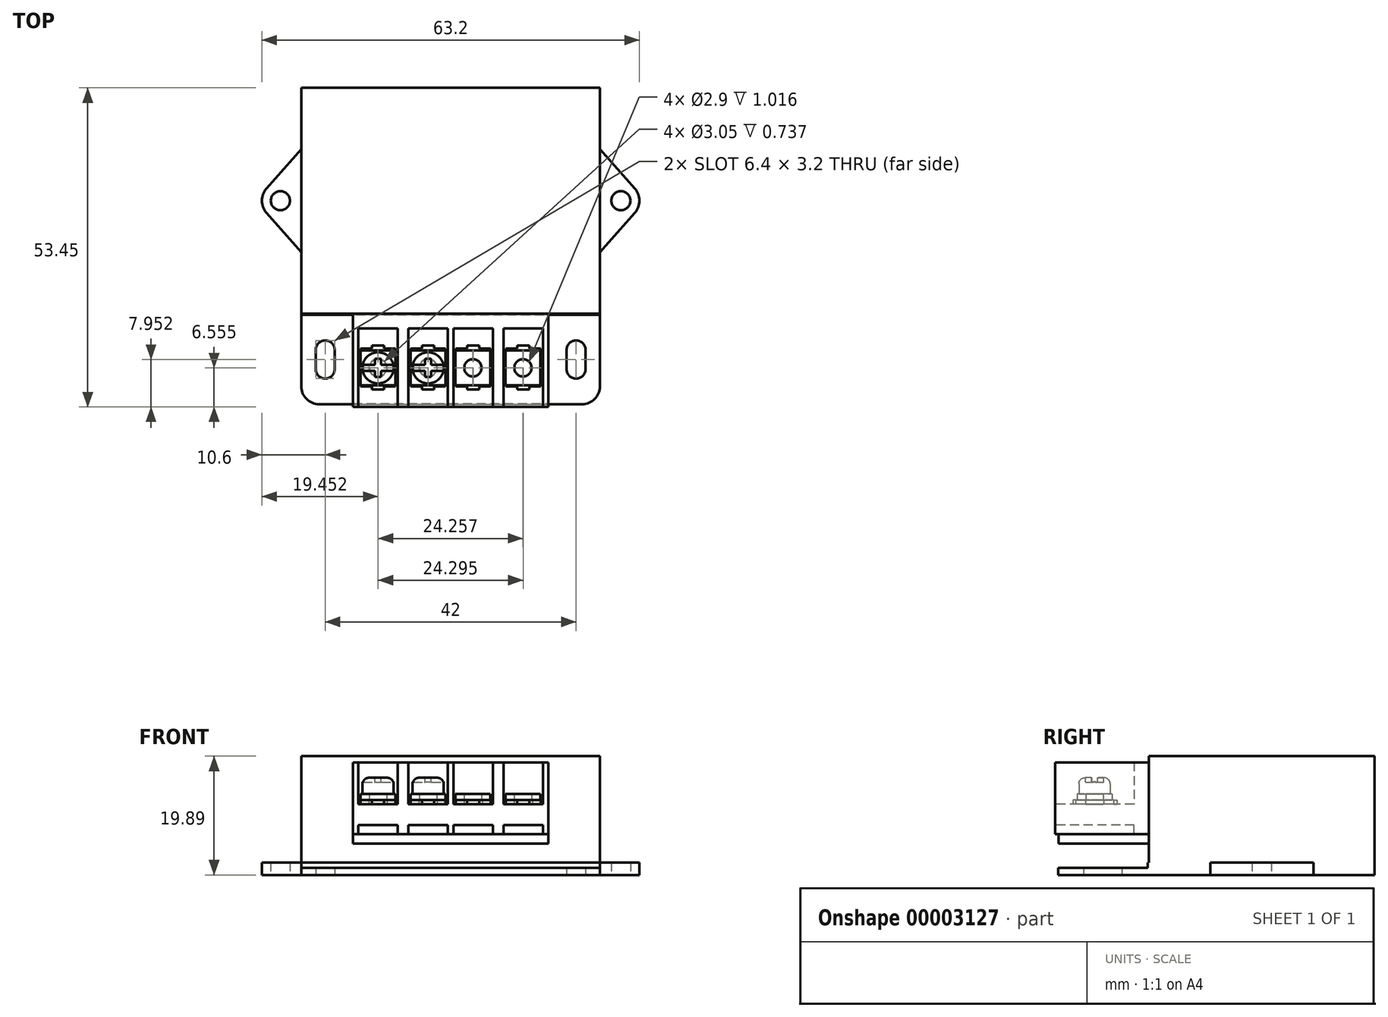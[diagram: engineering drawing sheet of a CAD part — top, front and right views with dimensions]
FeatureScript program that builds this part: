
annotation { "Feature Type Name" : "Feature", "Feature Type Description" : "" }
export const myFeature = defineFeature(function(context is Context, id is Id, definition is map)
    precondition{}
    {
        {
            var Q0;
            Q0=qCreatedBy(makeId("Top.planeOp"),FACE);
            var sketch = newSketch(context, id + "F0", { "sketchPlane" : qUnion([Q0])});
            skLineSegment(sketch, "E0.rect.bottom", {"start": v(0, -19.1) * mm, "end": v(-25, -19.1) * mm});
            skLineSegment(sketch, "E0.rect.top", {"start": v(0, 18.9) * mm, "end": v(-25, 18.9) * mm});
            skLineSegment(sketch, "E0.rect.right", {"start": v(-25, -19.1) * mm, "end": v(-25, -8.64) * mm});
            skPoint(sketch, "E0.rect.middle", {"position": v(0, 0) * mm});
            skLineSegment(sketch, "E1", {"start": v(0, 28.46) * mm, "end": v(0, -30.31) * mm, "construction": true});
            skLineSegment(sketch, "E2", {"start": v(-25, 8.64) * mm, "end": v(-30.82, 2.05) * mm});
            skLineSegment(sketch, "E3", {"start": v(-30.82, -2.05) * mm, "end": v(-25, -8.64) * mm});
            skCircle(sketch, "E4", {"center": v(-28.5, 0) * mm, "radius": 1.6 * mm});
            skArc(sketch, "E5", {"start": v(-30.82, 2.05) * mm, "mid": v(-31.6, 0) * mm, "end": v(-30.82, -2.05) * mm});
            skArc(sketch, "E6.0.MirrorCS", {"start": v(30.82, 2.05) * mm, "mid": v(31.6, 0) * mm, "end": v(30.82, -2.05) * mm});
            skCircle(sketch, "E6.1.MirrorC", {"center": v(28.5, 0) * mm, "radius": 1.6 * mm});
            skLineSegment(sketch, "E6.2.MirrorCS", {"start": v(25, -19.1) * mm, "end": v(25, -8.64) * mm});
            skLineSegment(sketch, "E6.3.MirrorCS", {"start": v(25, 8.64) * mm, "end": v(30.82, 2.05) * mm});
            skLineSegment(sketch, "E6.4.MirrorCS", {"start": v(30.82, -2.05) * mm, "end": v(25, -8.64) * mm});
            skLineSegment(sketch, "E7.0.MirrorCS", {"start": v(0, 18.9) * mm, "end": v(25, 18.9) * mm});
            skLineSegment(sketch, "E8.0.MirrorCS", {"start": v(0, -19.1) * mm, "end": v(25, -19.1) * mm});
            skLineSegment(sketch, "E9.trimOffspring", {"start": v(-25, 8.64) * mm, "end": v(-25, 18.9) * mm});
            skLineSegment(sketch, "E10.trimOffspring", {"start": v(25, 8.64) * mm, "end": v(25, 18.9) * mm});
            skSolve(sketch);
        }
        {
            var Q0;
            Q0=makeQuery(id+"F0.imprint","IMPRINT",FACE,{"disambiguationData":[TD([[makeQuery(id+"F0.imprint","IMPRINT",EDGE,{"derivedFrom":sQuery(id+"F0.wireOp",EDGE,"E0.rect.bottom")}),-1.0]])]});
            extrude(context, id + "F1", {"entities" : qUnion([Q0]), "depth" : 2.08 * mm});
        }
        {
            var Q0;
            Q0=makeQuery(id+"F1.opExtrude","CAP_FACE",FACE,{"disambiguationData":[OSD([sQuery(id+"F0.wireOp",EDGE,"E0.rect.bottom"),sQuery(id+"F0.wireOp",EDGE,"E0.rect.right"),sQuery(id+"F0.wireOp",EDGE,"E2"),sQuery(id+"F0.wireOp",EDGE,"E3"),sQuery(id+"F0.wireOp",EDGE,"E4"),sQuery(id+"F0.wireOp",EDGE,"E5"),sQuery(id+"F0.wireOp",EDGE,"E6.0.MirrorCS"),sQuery(id+"F0.wireOp",EDGE,"E6.1.MirrorC"),sQuery(id+"F0.wireOp",EDGE,"E6.2.MirrorCS"),sQuery(id+"F0.wireOp",EDGE,"E6.3.MirrorCS"),sQuery(id+"F0.wireOp",EDGE,"E6.4.MirrorCS"),sQuery(id+"F0.wireOp",EDGE,"E7.0.MirrorCS"),sQuery(id+"F0.wireOp",EDGE,"E9.trimOffspring"),sQuery(id+"F0.wireOp",EDGE,"E10.trimOffspring")])],"isStart":false});
            var sketch = newSketch(context, id + "F2", { "sketchPlane" : qUnion([Q0])});
            skLineSegment(sketch, "E11.rect.bottom", {"start": v(25, 18.9) * mm, "end": v(-25, 18.9) * mm});
            skLineSegment(sketch, "E11.rect.top", {"start": v(25, -18.9) * mm, "end": v(-25, -18.9) * mm});
            skLineSegment(sketch, "E11.rect.left", {"start": v(25, 18.9) * mm, "end": v(25, -18.9) * mm});
            skLineSegment(sketch, "E11.rect.right", {"start": v(-25, 18.9) * mm, "end": v(-25, -18.9) * mm});
            skPoint(sketch, "E11.rect.middle", {"position": v(0, 0) * mm});
            skSolve(sketch);
        }
        {
            var Q0;
            {var subQ2=sQuery(id+"F2.wireOp",EDGE,"E11.rect.bottom");Q0=makeQuery(id+"F2.imprint","IMPRINT",FACE,{"disambiguationData":[TD([[makeQuery(id+"F2.imprint","IMPRINT",EDGE,{"derivedFrom":subQ2}),-1.0]])]});}
            extrude(context, id + "F3", {"entities" : qUnion([Q0]), "operationType" : NewBodyOperationType.ADD, "depth" : 17.8 * mm});
        }
        {
            var Q0;
            Q0=qCreatedBy(makeId("Top.planeOp"),FACE);
            var sketch = newSketch(context, id + "F4", { "sketchPlane" : qUnion([Q0])});
            skLineSegment(sketch, "E12.bottom", {"start": v(-25, -19.1) * mm, "end": v(0, -19.1) * mm});
            skLineSegment(sketch, "E12.top", {"start": v(-22, -34.1) * mm, "end": v(0, -34.1) * mm});
            skLineSegment(sketch, "E12.left", {"start": v(-25, -19.1) * mm, "end": v(-25, -31.1) * mm});
            skPoint(sketch, "E13.visualSharp", {"position": v(-25, -34.1) * mm});
            skArc(sketch, "E13.filletArc", {"start": v(-25, -31.1) * mm, "mid": v(-24.12, -33.22) * mm, "end": v(-22, -34.1) * mm});
            skLineSegment(sketch, "E14", {"start": v(0, 0) * mm, "end": v(0, -41.86) * mm, "construction": true});
            skArc(sketch, "E15", {"start": v(-19.4, -25) * mm, "mid": v(-21, -23.4) * mm, "end": v(-22.6, -25) * mm});
            skArc(sketch, "E16", {"start": v(-22.6, -28.2) * mm, "mid": v(-21, -29.8) * mm, "end": v(-19.4, -28.2) * mm});
            skLineSegment(sketch, "E17", {"start": v(-27.88, -26.6) * mm, "end": v(-15.03, -26.6) * mm, "construction": true});
            skLineSegment(sketch, "E18", {"start": v(-22.6, -25) * mm, "end": v(-22.6, -28.2) * mm});
            skLineSegment(sketch, "E19", {"start": v(-19.4, -25) * mm, "end": v(-19.4, -28.2) * mm});
            skLineSegment(sketch, "E20.0.MirrorCS", {"start": v(-25, -19.1) * mm, "end": v(-25, -7.1) * mm});
            skArc(sketch, "E21.0.MirrorCS", {"start": v(-25, -7.1) * mm, "mid": v(-24.12, -4.98) * mm, "end": v(-22, -4.1) * mm});
            skLineSegment(sketch, "E22.0.MirrorCS", {"start": v(-22, -4.1) * mm, "end": v(0, -4.1) * mm});
            skArc(sketch, "E23.0.MirrorCS", {"start": v(-22.6, -10) * mm, "mid": v(-21, -8.4) * mm, "end": v(-19.4, -10) * mm});
            skLineSegment(sketch, "E24.0.MirrorCS", {"start": v(-19.4, -13.2) * mm, "end": v(-19.4, -10) * mm});
            skArc(sketch, "E25.0.MirrorCS", {"start": v(-19.4, -13.2) * mm, "mid": v(-21, -14.8) * mm, "end": v(-22.6, -13.2) * mm});
            skLineSegment(sketch, "E26.0.MirrorCS", {"start": v(22, -34.1) * mm, "end": v(0, -34.1) * mm});
            skArc(sketch, "E26.1.MirrorCS", {"start": v(25, -31.1) * mm, "mid": v(24.12, -33.22) * mm, "end": v(22, -34.1) * mm});
            skArc(sketch, "E26.2.MirrorCS", {"start": v(22.6, -28.2) * mm, "mid": v(21, -29.8) * mm, "end": v(19.4, -28.2) * mm});
            skLineSegment(sketch, "E26.3.MirrorCS", {"start": v(19.4, -25) * mm, "end": v(19.4, -28.2) * mm});
            skLineSegment(sketch, "E26.4.MirrorCS", {"start": v(22.6, -25) * mm, "end": v(22.6, -28.2) * mm});
            skArc(sketch, "E26.5.MirrorCS", {"start": v(19.4, -25) * mm, "mid": v(21, -23.4) * mm, "end": v(22.6, -25) * mm});
            skLineSegment(sketch, "E26.6.MirrorCS", {"start": v(25, -19.1) * mm, "end": v(0, -19.1) * mm});
            skLineSegment(sketch, "E26.7.MirrorCS", {"start": v(25, -19.1) * mm, "end": v(25, -31.1) * mm});
            skSolve(sketch);
        }
        {
            var Q0;
            Q0=makeQuery(id+"F4.imprint","IMPRINT",FACE,{"disambiguationData":[TD([[makeQuery(id+"F4.imprint","IMPRINT",EDGE,{"derivedFrom":sQuery(id+"F4.wireOp",EDGE,"E12.bottom")}),-1.0]])]});
            extrude(context, id + "F5", {"entities" : qUnion([Q0]), "operationType" : NewBodyOperationType.ADD, "depth" : 1.2 * mm});
        }
        {
            var Q0;
            Q0=makeQuery(id+"F3.opExtrude","SWEPT_FACE",FACE,{"disambiguationData":[OSD([sQuery(id+"F2.wireOp",EDGE,"E11.rect.top")])]});
            var sketch = newSketch(context, id + "F6", { "sketchPlane" : qUnion([Q0])});
            skLineSegment(sketch, "E27.bottom", {"start": v(-16.34, 18.85) * mm, "end": v(0, 18.85) * mm});
            skLineSegment(sketch, "E27.top", {"start": v(-16.34, 6.86) * mm, "end": v(0, 6.86) * mm});
            skLineSegment(sketch, "E27.left", {"start": v(-16.34, 18.85) * mm, "end": v(-16.34, 6.86) * mm});
            skLineSegment(sketch, "E28", {"start": v(0, 2.87) * mm, "end": v(0, 22.04) * mm, "construction": true});
            skLineSegment(sketch, "E29.0.MirrorCS", {"start": v(16.34, 18.85) * mm, "end": v(0, 18.85) * mm});
            skLineSegment(sketch, "E30.0.MirrorCS", {"start": v(16.34, 18.85) * mm, "end": v(16.34, 6.86) * mm});
            skLineSegment(sketch, "E31.0.MirrorCS", {"start": v(16.34, 6.86) * mm, "end": v(0, 6.86) * mm});
            skSolve(sketch);
        }
        {
            var Q0;
            Q0=makeQuery(id+"F6.imprint","IMPRINT",FACE,{"disambiguationData":[TD([[makeQuery(id+"F6.imprint","IMPRINT",EDGE,{"derivedFrom":sQuery(id+"F6.wireOp",EDGE,"E27.bottom")}),-1.0]])]});
            extrude(context, id + "F7", {"entities" : qUnion([Q0]), "depth" : 15.65 * mm});
        }
        {
            var Q0;
            Q0=makeQuery(id+"F7.opExtrude","CAP_FACE",FACE,{"disambiguationData":[OSD([sQuery(id+"F6.wireOp",EDGE,"E27.bottom"),sQuery(id+"F6.wireOp",EDGE,"E27.top"),sQuery(id+"F6.wireOp",EDGE,"E27.left"),sQuery(id+"F6.wireOp",EDGE,"E29.0.MirrorCS"),sQuery(id+"F6.wireOp",EDGE,"E30.0.MirrorCS"),sQuery(id+"F6.wireOp",EDGE,"E31.0.MirrorCS")])],"isStart":false});
            var sketch = newSketch(context, id + "F8", { "sketchPlane" : qUnion([Q0])});
            skLineSegment(sketch, "E32.bottom", {"start": v(-15.45, 18.85) * mm, "end": v(-8.85, 18.85) * mm});
            skLineSegment(sketch, "E32.top", {"start": v(-15.45, 11.84) * mm, "end": v(-8.85, 11.84) * mm});
            skLineSegment(sketch, "E32.left", {"start": v(-15.45, 18.85) * mm, "end": v(-15.45, 11.84) * mm});
            skLineSegment(sketch, "E32.right", {"start": v(-8.85, 18.85) * mm, "end": v(-8.85, 11.84) * mm});
            skLineSegment(sketch, "E33.bottom", {"start": v(-7.07, 18.85) * mm, "end": v(-0.46, 18.85) * mm});
            skLineSegment(sketch, "E33.top", {"start": v(-7.07, 11.84) * mm, "end": v(-0.46, 11.84) * mm});
            skLineSegment(sketch, "E33.left", {"start": v(-7.07, 18.85) * mm, "end": v(-7.07, 11.84) * mm});
            skLineSegment(sketch, "E33.right", {"start": v(-0.46, 18.85) * mm, "end": v(-0.46, 11.84) * mm});
            skLineSegment(sketch, "E34", {"start": v(0, 23) * mm, "end": v(0, -5.26) * mm, "construction": true});
            skLineSegment(sketch, "E35.0.MirrorCS", {"start": v(7.07, 18.85) * mm, "end": v(0.46, 18.85) * mm});
            skLineSegment(sketch, "E36.0.MirrorCS", {"start": v(7.07, 18.85) * mm, "end": v(7.07, 11.84) * mm});
            skLineSegment(sketch, "E37.0.MirrorCS", {"start": v(0.46, 18.85) * mm, "end": v(0.46, 11.84) * mm});
            skLineSegment(sketch, "E38.0.MirrorCS", {"start": v(7.07, 11.84) * mm, "end": v(0.46, 11.84) * mm});
            skLineSegment(sketch, "E39.0.MirrorCS", {"start": v(8.85, 18.85) * mm, "end": v(8.85, 11.84) * mm});
            skLineSegment(sketch, "E40.0.MirrorCS", {"start": v(15.45, 18.85) * mm, "end": v(8.85, 18.85) * mm});
            skLineSegment(sketch, "E41.0.MirrorCS", {"start": v(15.45, 18.85) * mm, "end": v(15.45, 11.84) * mm});
            skLineSegment(sketch, "E42.0.MirrorCS", {"start": v(15.45, 11.84) * mm, "end": v(8.85, 11.84) * mm});
            skLineSegment(sketch, "E43.bottom", {"start": v(-15.45, 6.86) * mm, "end": v(-8.85, 6.86) * mm});
            skLineSegment(sketch, "E43.top", {"start": v(-15.45, 8.36) * mm, "end": v(-8.85, 8.36) * mm});
            skLineSegment(sketch, "E43.left", {"start": v(-15.45, 6.86) * mm, "end": v(-15.45, 8.36) * mm});
            skLineSegment(sketch, "E43.right", {"start": v(-8.85, 6.86) * mm, "end": v(-8.85, 8.36) * mm});
            skLineSegment(sketch, "E44.bottom", {"start": v(-7.07, 6.86) * mm, "end": v(-0.46, 6.86) * mm});
            skLineSegment(sketch, "E44.top", {"start": v(-7.07, 8.36) * mm, "end": v(-0.46, 8.36) * mm});
            skLineSegment(sketch, "E44.left", {"start": v(-7.07, 6.86) * mm, "end": v(-7.07, 8.36) * mm});
            skLineSegment(sketch, "E44.right", {"start": v(-0.46, 6.86) * mm, "end": v(-0.46, 8.36) * mm});
            skLineSegment(sketch, "E45.0.MirrorCS", {"start": v(15.45, 6.86) * mm, "end": v(8.85, 6.86) * mm});
            skLineSegment(sketch, "E45.1.MirrorCS", {"start": v(0.46, 6.86) * mm, "end": v(0.46, 8.36) * mm});
            skLineSegment(sketch, "E45.2.MirrorCS", {"start": v(7.07, 6.86) * mm, "end": v(7.07, 8.36) * mm});
            skLineSegment(sketch, "E45.3.MirrorCS", {"start": v(15.45, 6.86) * mm, "end": v(15.45, 8.36) * mm});
            skLineSegment(sketch, "E45.4.MirrorCS", {"start": v(15.45, 8.36) * mm, "end": v(8.85, 8.36) * mm});
            skLineSegment(sketch, "E45.5.MirrorCS", {"start": v(7.07, 6.86) * mm, "end": v(0.46, 6.86) * mm});
            skLineSegment(sketch, "E45.6.MirrorCS", {"start": v(7.07, 8.36) * mm, "end": v(0.46, 8.36) * mm});
            skLineSegment(sketch, "E45.7.MirrorCS", {"start": v(8.85, 6.86) * mm, "end": v(8.85, 8.36) * mm});
            skSolve(sketch);
        }
        {
            var Q0;
            {Q0=qUnion([makeQuery(id+"F8.imprint","IMPRINT",FACE,{"disambiguationData":[TD([[makeQuery(id+"F8.imprint","IMPRINT",EDGE,{"derivedFrom":sQuery(id+"F8.wireOp",EDGE,"E32.bottom")}),-1.0]])]}),makeQuery(id+"F8.imprint","IMPRINT",FACE,{"disambiguationData":[TD([[makeQuery(id+"F8.imprint","IMPRINT",EDGE,{"derivedFrom":sQuery(id+"F8.wireOp",EDGE,"E33.bottom")}),-1.0]])]}),makeQuery(id+"F8.imprint","IMPRINT",FACE,{"disambiguationData":[TD([[makeQuery(id+"F8.imprint","IMPRINT",EDGE,{"derivedFrom":sQuery(id+"F8.wireOp",EDGE,"E35.0.MirrorCS")}),-1.0]])]}),makeQuery(id+"F8.imprint","IMPRINT",FACE,{"disambiguationData":[TD([[makeQuery(id+"F8.imprint","IMPRINT",EDGE,{"derivedFrom":sQuery(id+"F8.wireOp",EDGE,"E39.0.MirrorCS")}),1.0]])]}),makeQuery(id+"F8.imprint","IMPRINT",FACE,{"disambiguationData":[TD([[makeQuery(id+"F8.imprint","IMPRINT",EDGE,{"derivedFrom":sQuery(id+"F8.wireOp",EDGE,"E43.bottom")}),1.0]])]}),makeQuery(id+"F8.imprint","IMPRINT",FACE,{"disambiguationData":[TD([[makeQuery(id+"F8.imprint","IMPRINT",EDGE,{"derivedFrom":sQuery(id+"F8.wireOp",EDGE,"E44.bottom")}),1.0]])]}),makeQuery(id+"F8.imprint","IMPRINT",FACE,{"disambiguationData":[TD([[makeQuery(id+"F8.imprint","IMPRINT",EDGE,{"derivedFrom":sQuery(id+"F8.wireOp",EDGE,"E45.0.MirrorCS")}),1.0]])]}),makeQuery(id+"F8.imprint","IMPRINT",FACE,{"disambiguationData":[TD([[makeQuery(id+"F8.imprint","IMPRINT",EDGE,{"derivedFrom":sQuery(id+"F8.wireOp",EDGE,"E45.1.MirrorCS")}),-1.0]])]})]);}
            extrude(context, id + "F9", {"entities" : qUnion([Q0]), "operationType" : NewBodyOperationType.REMOVE, "oppositeDirection" : true, "depth" : 13.16 * mm});
        }
        {
            var Q0;
            Q0=makeQuery(id+"F3.opExtrude","SWEPT_FACE",FACE,{"disambiguationData":[OSD([sQuery(id+"F2.wireOp",EDGE,"E11.rect.top")])]});
            var sketch = newSketch(context, id + "F10", { "sketchPlane" : qUnion([Q0])});
            skLineSegment(sketch, "E46", {"start": v(0, 20.95) * mm, "end": v(0, -1.51) * mm, "construction": true});
            skLineSegment(sketch, "E47", {"start": v(0, 6.86) * mm, "end": v(-16.33, 6.86) * mm});
            skLineSegment(sketch, "E48", {"start": v(-16.33, 6.86) * mm, "end": v(-16.33, 5.23) * mm});
            skLineSegment(sketch, "E49", {"start": v(-16.33, 5.23) * mm, "end": v(0, 5.23) * mm});
            skLineSegment(sketch, "E50.0.MirrorCS", {"start": v(16.33, 5.23) * mm, "end": v(0, 5.23) * mm});
            skLineSegment(sketch, "E51.0.MirrorCS", {"start": v(0, 6.86) * mm, "end": v(16.33, 6.86) * mm});
            skLineSegment(sketch, "E52.0.MirrorCS", {"start": v(16.33, 6.86) * mm, "end": v(16.33, 5.23) * mm});
            skSolve(sketch);
        }
        {
            var Q0;
            Q0=makeQuery(id+"F10.imprint","IMPRINT",FACE,{"disambiguationData":[TD([[makeQuery(id+"F10.imprint","IMPRINT",EDGE,{"derivedFrom":sQuery(id+"F10.wireOp",EDGE,"E47")}),1.0]])]});
            var Q1;
            Q1=makeQuery(id+"F7.opExtrude","CAP_FACE",FACE,{"disambiguationData":[OSD([sQuery(id+"F6.wireOp",EDGE,"E27.bottom"),sQuery(id+"F6.wireOp",EDGE,"E27.top"),sQuery(id+"F6.wireOp",EDGE,"E27.left"),sQuery(id+"F6.wireOp",EDGE,"E29.0.MirrorCS"),sQuery(id+"F6.wireOp",EDGE,"E30.0.MirrorCS"),sQuery(id+"F6.wireOp",EDGE,"E31.0.MirrorCS")])],"isStart":false});
            extrude(context, id + "F11", {"entities" : qUnion([Q0]), "endBoundEntity" : qUnion([Q1]), "depth" : 15.1 * mm});
        }
        {
            var Q0;
            Q0=makeQuery(id+"F9.boolean.opBoolean","COPY",FACE,{"derivedFrom":makeQuery(id+"F9.opExtrude","SWEPT_FACE",FACE,{"disambiguationData":[OSD([sQuery(id+"F8.wireOp",EDGE,"E32.top")])]})});
            var sketch = newSketch(context, id + "F12", { "sketchPlane" : qUnion([Q0])});
            skLineSegment(sketch, "E53.bottom", {"start": v(-15.07, -24.77) * mm, "end": v(-13.16, -24.77) * mm});
            skLineSegment(sketch, "E53.top", {"start": v(-15.07, -31.12) * mm, "end": v(-13.16, -31.12) * mm});
            skLineSegment(sketch, "E53.left", {"start": v(-15.07, -24.77) * mm, "end": v(-15.07, -31.12) * mm});
            skLineSegment(sketch, "E53.right", {"start": v(-9.23, -24.77) * mm, "end": v(-9.23, -31.12) * mm});
            skLineSegment(sketch, "E54.bottom", {"start": v(-6.69, -24.77) * mm, "end": v(-4.78, -24.77) * mm});
            skLineSegment(sketch, "E54.top", {"start": v(-6.69, -31.12) * mm, "end": v(-4.78, -31.12) * mm});
            skLineSegment(sketch, "E54.left", {"start": v(-6.69, -24.77) * mm, "end": v(-6.69, -31.12) * mm});
            skLineSegment(sketch, "E54.right", {"start": v(-0.84, -24.77) * mm, "end": v(-0.84, -31.12) * mm});
            skLineSegment(sketch, "E55", {"start": v(-12.15, -21.4) * mm, "end": v(-12.15, -41.65) * mm, "construction": true});
            skLineSegment(sketch, "E56", {"start": v(-3.77, -21.7) * mm, "end": v(-3.77, -39.4) * mm, "construction": true});
            skLineSegment(sketch, "E57", {"start": v(0, -15.65) * mm, "end": v(0, -38.77) * mm, "construction": true});
            skLineSegment(sketch, "E58.top", {"start": v(-13.16, -24.26) * mm, "end": v(-11.13, -24.26) * mm});
            skLineSegment(sketch, "E58.left", {"start": v(-13.16, -24.77) * mm, "end": v(-13.16, -24.26) * mm});
            skLineSegment(sketch, "E58.right", {"start": v(-11.13, -24.77) * mm, "end": v(-11.13, -24.26) * mm});
            skLineSegment(sketch, "E59.top", {"start": v(-13.16, -31.63) * mm, "end": v(-11.13, -31.63) * mm});
            skLineSegment(sketch, "E59.left", {"start": v(-13.16, -31.12) * mm, "end": v(-13.16, -31.63) * mm});
            skLineSegment(sketch, "E59.right", {"start": v(-11.13, -31.12) * mm, "end": v(-11.13, -31.63) * mm});
            skLineSegment(sketch, "E60.top", {"start": v(-4.78, -24.26) * mm, "end": v(-2.75, -24.26) * mm});
            skLineSegment(sketch, "E60.left", {"start": v(-4.78, -24.77) * mm, "end": v(-4.78, -24.26) * mm});
            skLineSegment(sketch, "E60.right", {"start": v(-2.75, -24.77) * mm, "end": v(-2.75, -24.26) * mm});
            skLineSegment(sketch, "E61.top", {"start": v(-4.78, -31.63) * mm, "end": v(-2.75, -31.63) * mm});
            skLineSegment(sketch, "E61.left", {"start": v(-4.78, -31.12) * mm, "end": v(-4.78, -31.63) * mm});
            skLineSegment(sketch, "E61.right", {"start": v(-2.75, -31.12) * mm, "end": v(-2.75, -31.63) * mm});
            skLineSegment(sketch, "E62.trimOffspring", {"start": v(-11.13, -24.77) * mm, "end": v(-9.23, -24.77) * mm});
            skLineSegment(sketch, "E63.trimOffspring", {"start": v(-11.13, -31.12) * mm, "end": v(-9.23, -31.12) * mm});
            skLineSegment(sketch, "E64.trimOffspring", {"start": v(-2.75, -31.12) * mm, "end": v(-0.84, -31.12) * mm});
            skLineSegment(sketch, "E65.trimOffspring", {"start": v(-2.75, -24.77) * mm, "end": v(-0.84, -24.77) * mm});
            skLineSegment(sketch, "E66.0.MirrorCS", {"start": v(11.13, -31.12) * mm, "end": v(11.13, -31.63) * mm});
            skLineSegment(sketch, "E66.1.MirrorCS", {"start": v(2.75, -24.77) * mm, "end": v(0.84, -24.77) * mm});
            skLineSegment(sketch, "E66.2.MirrorCS", {"start": v(2.75, -31.12) * mm, "end": v(2.75, -31.63) * mm});
            skLineSegment(sketch, "E66.3.MirrorCS", {"start": v(11.13, -31.12) * mm, "end": v(9.23, -31.12) * mm});
            skLineSegment(sketch, "E66.4.MirrorCS", {"start": v(11.13, -24.77) * mm, "end": v(11.13, -24.26) * mm});
            skLineSegment(sketch, "E66.5.MirrorCS", {"start": v(4.78, -24.77) * mm, "end": v(4.78, -24.26) * mm});
            skLineSegment(sketch, "E66.6.MirrorCS", {"start": v(4.78, -31.63) * mm, "end": v(2.75, -31.63) * mm});
            skLineSegment(sketch, "E66.7.MirrorCS", {"start": v(4.78, -31.12) * mm, "end": v(4.78, -31.63) * mm});
            skLineSegment(sketch, "E66.8.MirrorCS", {"start": v(13.16, -24.26) * mm, "end": v(11.13, -24.26) * mm});
            skLineSegment(sketch, "E66.9.MirrorCS", {"start": v(6.69, -24.77) * mm, "end": v(6.69, -31.12) * mm});
            skLineSegment(sketch, "E66.10.MirrorCS", {"start": v(0.84, -24.77) * mm, "end": v(0.84, -31.12) * mm});
            skLineSegment(sketch, "E66.11.MirrorCS", {"start": v(13.16, -31.63) * mm, "end": v(11.13, -31.63) * mm});
            skLineSegment(sketch, "E66.12.MirrorCS", {"start": v(6.69, -24.77) * mm, "end": v(4.78, -24.77) * mm});
            skLineSegment(sketch, "E66.13.MirrorCS", {"start": v(6.69, -31.12) * mm, "end": v(4.78, -31.12) * mm});
            skLineSegment(sketch, "E66.14.MirrorCS", {"start": v(15.07, -24.77) * mm, "end": v(15.07, -31.12) * mm});
            skLineSegment(sketch, "E66.15.MirrorCS", {"start": v(2.75, -31.12) * mm, "end": v(0.84, -31.12) * mm});
            skLineSegment(sketch, "E66.16.MirrorCS", {"start": v(11.13, -24.77) * mm, "end": v(9.23, -24.77) * mm});
            skLineSegment(sketch, "E66.17.MirrorCS", {"start": v(13.16, -24.77) * mm, "end": v(13.16, -24.26) * mm});
            skLineSegment(sketch, "E66.18.MirrorCS", {"start": v(13.16, -31.12) * mm, "end": v(13.16, -31.63) * mm});
            skLineSegment(sketch, "E66.19.MirrorCS", {"start": v(15.07, -24.77) * mm, "end": v(13.16, -24.77) * mm});
            skLineSegment(sketch, "E66.20.MirrorCS", {"start": v(9.23, -24.77) * mm, "end": v(9.23, -31.12) * mm});
            skLineSegment(sketch, "E66.21.MirrorCS", {"start": v(4.78, -24.26) * mm, "end": v(2.75, -24.26) * mm});
            skLineSegment(sketch, "E66.22.MirrorCS", {"start": v(15.07, -31.12) * mm, "end": v(13.16, -31.12) * mm});
            skLineSegment(sketch, "E66.23.MirrorCS", {"start": v(2.75, -24.77) * mm, "end": v(2.75, -24.26) * mm});
            skCircle(sketch, "E67", {"center": v(-12.15, -28) * mm, "radius": 1.52 * mm});
            skCircle(sketch, "E68", {"center": v(-3.77, -28) * mm, "radius": 1.52 * mm});
            skCircle(sketch, "E69", {"center": v(3.77, -28) * mm, "radius": 1.52 * mm});
            skCircle(sketch, "E70", {"center": v(12.15, -28) * mm, "radius": 1.52 * mm});
            skSolve(sketch);
        }
        {
            var Q0;
            {Q0=qUnion([makeQuery(id+"F12.imprint","IMPRINT",FACE,{"disambiguationData":[TD([[makeQuery(id+"F12.imprint","IMPRINT",EDGE,{"derivedFrom":sQuery(id+"F12.wireOp",EDGE,"E54.bottom")}),-1.0]])]}),makeQuery(id+"F12.imprint","IMPRINT",FACE,{"disambiguationData":[TD([[makeQuery(id+"F12.imprint","IMPRINT",EDGE,{"derivedFrom":sQuery(id+"F12.wireOp",EDGE,"E66.0.MirrorCS")}),1.0]])]}),makeQuery(id+"F12.imprint","IMPRINT",FACE,{"disambiguationData":[TD([[makeQuery(id+"F12.imprint","IMPRINT",EDGE,{"derivedFrom":sQuery(id+"F12.wireOp",EDGE,"E66.1.MirrorCS")}),1.0]])]}),makeQuery(id+"F12.imprint","IMPRINT",FACE,{"disambiguationData":[TD([[makeQuery(id+"F12.imprint","IMPRINT",EDGE,{"derivedFrom":sQuery(id+"F12.wireOp",EDGE,"E53.bottom")}),-1.0]])]})]);}
            extrude(context, id + "F13", {"entities" : qUnion([Q0]), "operationType" : NewBodyOperationType.ADD, "depth" : 0.74 * mm});
        }
        {
            var Q0;
            Q0=makeQuery(id+"F13.opExtrude","CAP_FACE",FACE,{"disambiguationData":[OSD([sQuery(id+"F12.wireOp",EDGE,"E53.bottom"),sQuery(id+"F12.wireOp",EDGE,"E53.top"),sQuery(id+"F12.wireOp",EDGE,"E53.left"),sQuery(id+"F12.wireOp",EDGE,"E53.right"),sQuery(id+"F12.wireOp",EDGE,"E58.top"),sQuery(id+"F12.wireOp",EDGE,"E58.left"),sQuery(id+"F12.wireOp",EDGE,"E58.right"),sQuery(id+"F12.wireOp",EDGE,"E59.top"),sQuery(id+"F12.wireOp",EDGE,"E59.left"),sQuery(id+"F12.wireOp",EDGE,"E59.right"),sQuery(id+"F12.wireOp",EDGE,"E62.trimOffspring"),sQuery(id+"F12.wireOp",EDGE,"E63.trimOffspring"),sQuery(id+"F12.wireOp",EDGE,"E67")])],"isStart":false});
            var sketch = newSketch(context, id + "F14", { "sketchPlane" : qUnion([Q0])});
            skLineSegment(sketch, "E71.rect.bottom", {"start": v(-9.23, -30.92) * mm, "end": v(-15.07, -30.92) * mm});
            skLineSegment(sketch, "E71.rect.top", {"start": v(-9.23, -25.07) * mm, "end": v(-15.07, -25.07) * mm});
            skLineSegment(sketch, "E71.rect.left", {"start": v(-9.23, -30.92) * mm, "end": v(-9.23, -25.07) * mm});
            skLineSegment(sketch, "E71.rect.right", {"start": v(-15.07, -30.92) * mm, "end": v(-15.07, -25.07) * mm});
            skPoint(sketch, "E71.rect.middle", {"position": v(-12.15, -28) * mm});
            skLineSegment(sketch, "E72.rect.bottom", {"start": v(-0.84, -30.92) * mm, "end": v(-6.69, -30.92) * mm});
            skLineSegment(sketch, "E72.rect.top", {"start": v(-0.84, -25.07) * mm, "end": v(-6.69, -25.07) * mm});
            skLineSegment(sketch, "E72.rect.left", {"start": v(-0.84, -30.92) * mm, "end": v(-0.84, -25.07) * mm});
            skLineSegment(sketch, "E72.rect.right", {"start": v(-6.69, -30.92) * mm, "end": v(-6.69, -25.07) * mm});
            skPoint(sketch, "E72.rect.middle", {"position": v(-3.77, -28) * mm});
            skLineSegment(sketch, "E73.rect.bottom", {"start": v(6.65, -30.92) * mm, "end": v(0.8, -30.92) * mm});
            skLineSegment(sketch, "E73.rect.top", {"start": v(6.65, -25.07) * mm, "end": v(0.8, -25.07) * mm});
            skLineSegment(sketch, "E73.rect.left", {"start": v(6.65, -30.92) * mm, "end": v(6.65, -25.07) * mm});
            skLineSegment(sketch, "E73.rect.right", {"start": v(0.8, -30.92) * mm, "end": v(0.8, -25.07) * mm});
            skPoint(sketch, "E73.rect.middle", {"position": v(3.73, -28) * mm});
            skLineSegment(sketch, "E74.rect.bottom", {"start": v(15.03, -30.92) * mm, "end": v(9.19, -30.92) * mm});
            skLineSegment(sketch, "E74.rect.top", {"start": v(15.03, -25.07) * mm, "end": v(9.19, -25.07) * mm});
            skLineSegment(sketch, "E74.rect.left", {"start": v(15.03, -30.92) * mm, "end": v(15.03, -25.07) * mm});
            skLineSegment(sketch, "E74.rect.right", {"start": v(9.19, -30.92) * mm, "end": v(9.19, -25.07) * mm});
            skPoint(sketch, "E74.rect.middle", {"position": v(12.1, -28) * mm});
            skCircle(sketch, "E75", {"center": v(-12.15, -28) * mm, "radius": 1.45 * mm});
            skCircle(sketch, "E76", {"center": v(-3.77, -28) * mm, "radius": 1.45 * mm});
            skCircle(sketch, "E77", {"center": v(3.73, -28) * mm, "radius": 1.45 * mm});
            skCircle(sketch, "E78", {"center": v(12.1, -28) * mm, "radius": 1.45 * mm});
            skSolve(sketch);
        }
        {
            var Q0;
            {Q0=qUnion([makeQuery(id+"F14.imprint","IMPRINT",FACE,{"disambiguationData":[TD([[makeQuery(id+"F14.imprint","IMPRINT",EDGE,{"derivedFrom":sQuery(id+"F14.wireOp",EDGE,"E72.rect.bottom")}),-1.0]])]}),makeQuery(id+"F14.imprint","IMPRINT",FACE,{"disambiguationData":[TD([[makeQuery(id+"F14.imprint","IMPRINT",EDGE,{"derivedFrom":sQuery(id+"F14.wireOp",EDGE,"E73.rect.bottom")}),-1.0]])]}),makeQuery(id+"F14.imprint","IMPRINT",FACE,{"disambiguationData":[TD([[makeQuery(id+"F14.imprint","IMPRINT",EDGE,{"derivedFrom":sQuery(id+"F14.wireOp",EDGE,"E74.rect.bottom")}),-1.0]])]}),makeQuery(id+"F14.imprint","IMPRINT",FACE,{"disambiguationData":[TD([[makeQuery(id+"F14.imprint","IMPRINT",EDGE,{"derivedFrom":sQuery(id+"F14.wireOp",EDGE,"E75")}),-1.0]])]}),makeQuery(id+"F14.imprint","IMPRINT",FACE,{"disambiguationData":[TD([[makeQuery(id+"F14.imprint","IMPRINT",EDGE,{"derivedFrom":sQuery(id+"F14.wireOp",EDGE,"E71.rect.bottom")}),-1.0]])]})]);}
            extrude(context, id + "F15", {"entities" : qUnion([Q0]), "operationType" : NewBodyOperationType.ADD, "depth" : 1.02 * mm});
        }
        {
            var Q0;
            Q0=makeQuery(id+"F15.opExtrude","CAP_FACE",FACE,{"disambiguationData":[OSD([sQuery(id+"F14.wireOp",EDGE,"E71.rect.bottom"),sQuery(id+"F14.wireOp",EDGE,"E71.rect.top"),sQuery(id+"F14.wireOp",EDGE,"E71.rect.left"),sQuery(id+"F14.wireOp",EDGE,"E71.rect.right"),sQuery(id+"F14.wireOp",EDGE,"E75")])],"isStart":false});
            var sketch = newSketch(context, id + "F16", { "sketchPlane" : qUnion([Q0])});
            skCircle(sketch, "E79", {"center": v(-12.15, -28) * mm, "radius": 2.62 * mm});
            skCircle(sketch, "E80", {"center": v(-3.77, -28) * mm, "radius": 2.62 * mm});
            skLineSegment(sketch, "E81", {"start": v(0, -19.02) * mm, "end": v(0, -38.5) * mm, "construction": true});
            skCircle(sketch, "E82.0.MirrorC", {"center": v(3.77, -28) * mm, "radius": 2.62 * mm});
            skCircle(sketch, "E83.0.MirrorC", {"center": v(12.15, -28) * mm, "radius": 2.62 * mm});
            skSolve(sketch);
        }
        {
            var Q0;
            {var subQ0=makeQuery(id+"F16.imprint","IMPRINT",EDGE,{"derivedFrom":makeQuery(id+"F15.opExtrude","CAP_EDGE",EDGE,{"disambiguationData":[OSD([sQuery(id+"F14.wireOp",EDGE,"E75")])],"isStart":false})});Q0=qUnion([makeQuery(id+"F16.imprint","IMPRINT",FACE,{"disambiguationData":[TD([[makeQuery(id+"F16.imprint","IMPRINT",EDGE,{"derivedFrom":sQuery(id+"F16.wireOp",EDGE,"E80")}),1.0]])]}),makeQuery(id+"F16.imprint","IMPRINT",FACE,{"disambiguationData":[TD([[makeQuery(id+"F16.imprint","IMPRINT",EDGE,{"derivedFrom":sQuery(id+"F16.wireOp",EDGE,"E82.0.MirrorC")}),-1.0]])]}),makeQuery(id+"F16.imprint","IMPRINT",FACE,{"disambiguationData":[TD([[makeQuery(id+"F16.imprint","IMPRINT",EDGE,{"derivedFrom":sQuery(id+"F16.wireOp",EDGE,"E83.0.MirrorC")}),-1.0]])]}),makeQuery(id+"F16.imprint","IMPRINT",FACE,{"disambiguationData":[TD([[subQ0,1.0]])]}),makeQuery(id+"F16.imprint","IMPRINT",FACE,{"disambiguationData":[TD([[makeQuery(id+"F16.imprint","IMPRINT",EDGE,{"derivedFrom":sQuery(id+"F16.wireOp",EDGE,"E79")}),1.0]])]})]);}
            extrude(context, id + "F17", {"entities" : qUnion([Q0]), "operationType" : NewBodyOperationType.ADD, "depth" : 2.7 * mm});
        }
        {
            var Q0;
            Q0=makeQuery(id+"F17.opExtrude","CAP_FACE",FACE,{"disambiguationData":[OSD([sQuery(id+"F16.wireOp",EDGE,"E79")])],"isStart":false});
            var sketch = newSketch(context, id + "F18", { "sketchPlane" : qUnion([Q0])});
            skLineSegment(sketch, "E84.rect.bottom", {"start": v(-12.54, -26.47) * mm, "end": v(-11.76, -26.47) * mm});
            skLineSegment(sketch, "E84.rect.top", {"start": v(-12.54, -29.52) * mm, "end": v(-11.76, -29.52) * mm});
            skLineSegment(sketch, "E84.rect.left", {"start": v(-12.66, -26.59) * mm, "end": v(-12.66, -27.37) * mm});
            skLineSegment(sketch, "E84.rect.right", {"start": v(-11.64, -26.59) * mm, "end": v(-11.64, -27.37) * mm});
            skLineSegment(sketch, "E85.rect.bottom", {"start": v(-14.6, -27.49) * mm, "end": v(-12.77, -27.49) * mm});
            skLineSegment(sketch, "E85.rect.top", {"start": v(-14.6, -28.5) * mm, "end": v(-12.77, -28.5) * mm});
            skLineSegment(sketch, "E85.rect.left", {"start": v(-14.71, -27.6) * mm, "end": v(-14.71, -28.39) * mm});
            skLineSegment(sketch, "E85.rect.right", {"start": v(-9.58, -27.6) * mm, "end": v(-9.58, -28.39) * mm});
            skLineSegment(sketch, "E86.rect.bottom", {"start": v(-3.37, -29.52) * mm, "end": v(-4.16, -29.52) * mm});
            skLineSegment(sketch, "E86.rect.top", {"start": v(-3.37, -26.47) * mm, "end": v(-4.16, -26.47) * mm});
            skLineSegment(sketch, "E86.rect.left", {"start": v(-3.26, -29.4) * mm, "end": v(-3.26, -28.62) * mm});
            skLineSegment(sketch, "E86.rect.right", {"start": v(-4.27, -29.4) * mm, "end": v(-4.27, -28.62) * mm});
            skLineSegment(sketch, "E87.rect.bottom", {"start": v(-6.22, -27.49) * mm, "end": v(-4.39, -27.49) * mm});
            skLineSegment(sketch, "E87.rect.top", {"start": v(-6.22, -28.5) * mm, "end": v(-4.39, -28.5) * mm});
            skLineSegment(sketch, "E87.rect.left", {"start": v(-6.33, -27.6) * mm, "end": v(-6.33, -28.39) * mm});
            skLineSegment(sketch, "E87.rect.right", {"start": v(-1.2, -27.6) * mm, "end": v(-1.2, -28.39) * mm});
            skLineSegment(sketch, "E88.2.MirrorCS", {"start": v(9.58, -27.6) * mm, "end": v(9.58, -28.39) * mm});
            skLineSegment(sketch, "E88.3.MirrorCS", {"start": v(3.37, -29.52) * mm, "end": v(4.16, -29.52) * mm});
            skLineSegment(sketch, "E88.4.MirrorCS", {"start": v(3.37, -26.47) * mm, "end": v(4.27, -26.47) * mm});
            skLineSegment(sketch, "E88.5.MirrorCS", {"start": v(3.26, -29.4) * mm, "end": v(3.26, -28.62) * mm});
            skLineSegment(sketch, "E88.6.MirrorCS", {"start": v(4.27, -29.4) * mm, "end": v(4.27, -28.62) * mm});
            skLineSegment(sketch, "E88.7.MirrorCS", {"start": v(6.22, -27.49) * mm, "end": v(4.39, -27.49) * mm});
            skLineSegment(sketch, "E88.8.MirrorCS", {"start": v(12.54, -29.52) * mm, "end": v(11.76, -29.52) * mm});
            skLineSegment(sketch, "E88.9.MirrorCS", {"start": v(12.66, -26.59) * mm, "end": v(12.66, -27.37) * mm});
            skLineSegment(sketch, "E88.10.MirrorCS", {"start": v(11.64, -26.59) * mm, "end": v(11.64, -27.37) * mm});
            skLineSegment(sketch, "E88.11.MirrorCS", {"start": v(14.6, -27.49) * mm, "end": v(12.77, -27.49) * mm});
            skLineSegment(sketch, "E88.12.MirrorCS", {"start": v(14.6, -28.5) * mm, "end": v(12.66, -28.5) * mm});
            skLineSegment(sketch, "E88.13.MirrorCS", {"start": v(14.71, -27.6) * mm, "end": v(14.71, -28.39) * mm});
            skLineSegment(sketch, "E88.16.MirrorCS", {"start": v(6.33, -27.6) * mm, "end": v(6.33, -28.39) * mm});
            skLineSegment(sketch, "E88.17.MirrorCS", {"start": v(6.22, -28.5) * mm, "end": v(4.39, -28.5) * mm});
            skLineSegment(sketch, "E88.18.MirrorCS", {"start": v(1.2, -27.6) * mm, "end": v(1.2, -28.39) * mm});
            skLineSegment(sketch, "E88.19.MirrorCS", {"start": v(12.54, -26.47) * mm, "end": v(11.76, -26.47) * mm});
            skLineSegment(sketch, "E89.trimOffspring", {"start": v(-11.52, -27.49) * mm, "end": v(-9.7, -27.49) * mm});
            skLineSegment(sketch, "E90.trimOffspring", {"start": v(-12.66, -28.62) * mm, "end": v(-12.66, -29.4) * mm});
            skLineSegment(sketch, "E91.trimOffspring", {"start": v(-11.64, -28.62) * mm, "end": v(-11.64, -29.4) * mm});
            skLineSegment(sketch, "E92.trimOffspring", {"start": v(-11.52, -28.5) * mm, "end": v(-9.7, -28.5) * mm});
            skLineSegment(sketch, "E93.trimOffspring", {"start": v(-4.27, -27.37) * mm, "end": v(-4.27, -26.59) * mm});
            skLineSegment(sketch, "E94.trimOffspring", {"start": v(-3.14, -27.49) * mm, "end": v(-1.31, -27.49) * mm});
            skLineSegment(sketch, "E95.trimOffspring", {"start": v(-3.14, -28.5) * mm, "end": v(-1.31, -28.5) * mm});
            skLineSegment(sketch, "E96.trimOffspring", {"start": v(-3.26, -27.37) * mm, "end": v(-3.26, -26.59) * mm});
            skLineSegment(sketch, "E97.trimOffspring", {"start": v(3.26, -27.49) * mm, "end": v(3.26, -26.59) * mm});
            skLineSegment(sketch, "E98.trimOffspring", {"start": v(3.26, -27.49) * mm, "end": v(1.31, -27.49) * mm});
            skLineSegment(sketch, "E99.trimOffspring", {"start": v(4.27, -27.37) * mm, "end": v(4.27, -26.47) * mm});
            skLineSegment(sketch, "E100.trimOffspring", {"start": v(3.14, -28.5) * mm, "end": v(1.31, -28.5) * mm});
            skLineSegment(sketch, "E101.trimOffspring", {"start": v(11.64, -28.62) * mm, "end": v(11.64, -29.4) * mm});
            skLineSegment(sketch, "E102.trimOffspring", {"start": v(11.52, -27.49) * mm, "end": v(9.7, -27.49) * mm});
            skLineSegment(sketch, "E103.trimOffspring", {"start": v(11.52, -28.5) * mm, "end": v(9.7, -28.5) * mm});
            skLineSegment(sketch, "E104.trimOffspring", {"start": v(12.66, -28.5) * mm, "end": v(12.66, -29.4) * mm});
            skPoint(sketch, "E105.visualSharp", {"position": v(-12.66, -26.47) * mm});
            skArc(sketch, "E105.filletArc", {"start": v(-12.54, -26.47) * mm, "mid": v(-12.62, -26.5) * mm, "end": v(-12.66, -26.59) * mm});
            skPoint(sketch, "E106.visualSharp", {"position": v(-11.64, -26.47) * mm});
            skArc(sketch, "E106.filletArc", {"start": v(-11.64, -26.59) * mm, "mid": v(-11.67, -26.5) * mm, "end": v(-11.76, -26.47) * mm});
            skPoint(sketch, "E107.visualSharp", {"position": v(-11.64, -27.49) * mm});
            skArc(sketch, "E107.filletArc", {"start": v(-11.64, -27.37) * mm, "mid": v(-11.6, -27.45) * mm, "end": v(-11.52, -27.49) * mm});
            skPoint(sketch, "E108.visualSharp", {"position": v(-9.58, -27.49) * mm});
            skArc(sketch, "E108.filletArc", {"start": v(-9.58, -27.6) * mm, "mid": v(-9.62, -27.52) * mm, "end": v(-9.7, -27.49) * mm});
            skPoint(sketch, "E109.visualSharp", {"position": v(-9.58, -28.5) * mm});
            skArc(sketch, "E109.filletArc", {"start": v(-9.7, -28.5) * mm, "mid": v(-9.62, -28.47) * mm, "end": v(-9.58, -28.39) * mm});
            skPoint(sketch, "E110.visualSharp", {"position": v(-14.71, -28.5) * mm});
            skArc(sketch, "E110.filletArc", {"start": v(-14.71, -28.39) * mm, "mid": v(-14.68, -28.47) * mm, "end": v(-14.6, -28.5) * mm});
            skPoint(sketch, "E111.visualSharp", {"position": v(-14.71, -27.49) * mm});
            skArc(sketch, "E111.filletArc", {"start": v(-14.6, -27.49) * mm, "mid": v(-14.68, -27.52) * mm, "end": v(-14.71, -27.6) * mm});
            skPoint(sketch, "E112.visualSharp", {"position": v(-6.33, -27.49) * mm});
            skArc(sketch, "E112.filletArc", {"start": v(-6.22, -27.49) * mm, "mid": v(-6.3, -27.52) * mm, "end": v(-6.33, -27.6) * mm});
            skPoint(sketch, "E113.visualSharp", {"position": v(-6.33, -28.5) * mm});
            skArc(sketch, "E113.filletArc", {"start": v(-6.33, -28.39) * mm, "mid": v(-6.3, -28.47) * mm, "end": v(-6.22, -28.5) * mm});
            skPoint(sketch, "E114.visualSharp", {"position": v(-4.27, -27.49) * mm});
            skArc(sketch, "E114.filletArc", {"start": v(-4.39, -27.49) * mm, "mid": v(-4.3, -27.45) * mm, "end": v(-4.27, -27.37) * mm});
            skPoint(sketch, "E115.visualSharp", {"position": v(-12.66, -27.49) * mm});
            skArc(sketch, "E115.filletArc", {"start": v(-12.77, -27.49) * mm, "mid": v(-12.69, -27.45) * mm, "end": v(-12.66, -27.37) * mm});
            skPoint(sketch, "E116.visualSharp", {"position": v(-12.66, -28.5) * mm});
            skArc(sketch, "E116.filletArc", {"start": v(-12.66, -28.62) * mm, "mid": v(-12.69, -28.54) * mm, "end": v(-12.77, -28.5) * mm});
            skPoint(sketch, "E117.visualSharp", {"position": v(-11.64, -28.5) * mm});
            skArc(sketch, "E117.filletArc", {"start": v(-11.52, -28.5) * mm, "mid": v(-11.6, -28.54) * mm, "end": v(-11.64, -28.62) * mm});
            skPoint(sketch, "E118.visualSharp", {"position": v(-4.27, -28.5) * mm});
            skArc(sketch, "E118.filletArc", {"start": v(-4.27, -28.62) * mm, "mid": v(-4.3, -28.54) * mm, "end": v(-4.39, -28.5) * mm});
            skPoint(sketch, "E119.visualSharp", {"position": v(-3.26, -28.5) * mm});
            skArc(sketch, "E119.filletArc", {"start": v(-3.14, -28.5) * mm, "mid": v(-3.22, -28.54) * mm, "end": v(-3.26, -28.62) * mm});
            skPoint(sketch, "E120.visualSharp", {"position": v(-3.26, -29.52) * mm});
            skArc(sketch, "E120.filletArc", {"start": v(-3.37, -29.52) * mm, "mid": v(-3.3, -29.49) * mm, "end": v(-3.26, -29.4) * mm});
            skPoint(sketch, "E121.visualSharp", {"position": v(-4.27, -29.52) * mm});
            skArc(sketch, "E121.filletArc", {"start": v(-4.27, -29.4) * mm, "mid": v(-4.24, -29.49) * mm, "end": v(-4.16, -29.52) * mm});
            skPoint(sketch, "E122.visualSharp", {"position": v(-1.2, -28.5) * mm});
            skArc(sketch, "E122.filletArc", {"start": v(-1.31, -28.5) * mm, "mid": v(-1.23, -28.47) * mm, "end": v(-1.2, -28.39) * mm});
            skPoint(sketch, "E123.visualSharp", {"position": v(-1.2, -27.49) * mm});
            skArc(sketch, "E123.filletArc", {"start": v(-1.2, -27.6) * mm, "mid": v(-1.23, -27.52) * mm, "end": v(-1.31, -27.49) * mm});
            skPoint(sketch, "E124.visualSharp", {"position": v(-3.26, -27.49) * mm});
            skArc(sketch, "E124.filletArc", {"start": v(-3.26, -27.37) * mm, "mid": v(-3.22, -27.45) * mm, "end": v(-3.14, -27.49) * mm});
            skPoint(sketch, "E125.visualSharp", {"position": v(-3.26, -26.47) * mm});
            skArc(sketch, "E125.filletArc", {"start": v(-3.26, -26.59) * mm, "mid": v(-3.3, -26.5) * mm, "end": v(-3.37, -26.47) * mm});
            skPoint(sketch, "E126.visualSharp", {"position": v(-4.27, -26.47) * mm});
            skArc(sketch, "E126.filletArc", {"start": v(-4.16, -26.47) * mm, "mid": v(-4.24, -26.5) * mm, "end": v(-4.27, -26.59) * mm});
            skPoint(sketch, "E127.visualSharp", {"position": v(-12.66, -29.52) * mm});
            skArc(sketch, "E127.filletArc", {"start": v(-12.66, -29.4) * mm, "mid": v(-12.62, -29.49) * mm, "end": v(-12.54, -29.52) * mm});
            skPoint(sketch, "E128.visualSharp", {"position": v(-11.64, -29.52) * mm});
            skArc(sketch, "E128.filletArc", {"start": v(-11.76, -29.52) * mm, "mid": v(-11.67, -29.49) * mm, "end": v(-11.64, -29.4) * mm});
            skPoint(sketch, "E129.visualSharp", {"position": v(14.71, -28.5) * mm});
            skArc(sketch, "E129.filletArc", {"start": v(14.6, -28.5) * mm, "mid": v(14.68, -28.47) * mm, "end": v(14.71, -28.39) * mm});
            skPoint(sketch, "E130.visualSharp", {"position": v(14.71, -27.49) * mm});
            skArc(sketch, "E130.filletArc", {"start": v(14.71, -27.6) * mm, "mid": v(14.68, -27.52) * mm, "end": v(14.6, -27.49) * mm});
            skPoint(sketch, "E131.visualSharp", {"position": v(12.66, -27.49) * mm});
            skArc(sketch, "E131.filletArc", {"start": v(12.66, -27.37) * mm, "mid": v(12.69, -27.45) * mm, "end": v(12.77, -27.49) * mm});
            skPoint(sketch, "E132.visualSharp", {"position": v(12.66, -26.47) * mm});
            skArc(sketch, "E132.filletArc", {"start": v(12.66, -26.59) * mm, "mid": v(12.62, -26.5) * mm, "end": v(12.54, -26.47) * mm});
            skPoint(sketch, "E133.visualSharp", {"position": v(11.64, -26.47) * mm});
            skArc(sketch, "E133.filletArc", {"start": v(11.76, -26.47) * mm, "mid": v(11.67, -26.5) * mm, "end": v(11.64, -26.59) * mm});
            skPoint(sketch, "E134.visualSharp", {"position": v(11.64, -27.49) * mm});
            skArc(sketch, "E134.filletArc", {"start": v(11.52, -27.49) * mm, "mid": v(11.6, -27.45) * mm, "end": v(11.64, -27.37) * mm});
            skPoint(sketch, "E135.visualSharp", {"position": v(9.58, -27.49) * mm});
            skArc(sketch, "E135.filletArc", {"start": v(9.7, -27.49) * mm, "mid": v(9.62, -27.52) * mm, "end": v(9.58, -27.6) * mm});
            skPoint(sketch, "E136.visualSharp", {"position": v(9.58, -28.5) * mm});
            skArc(sketch, "E136.filletArc", {"start": v(9.58, -28.39) * mm, "mid": v(9.62, -28.47) * mm, "end": v(9.7, -28.5) * mm});
            skPoint(sketch, "E137.visualSharp", {"position": v(11.64, -28.5) * mm});
            skArc(sketch, "E137.filletArc", {"start": v(11.64, -28.62) * mm, "mid": v(11.6, -28.54) * mm, "end": v(11.52, -28.5) * mm});
            skPoint(sketch, "E138.visualSharp", {"position": v(11.64, -29.52) * mm});
            skArc(sketch, "E138.filletArc", {"start": v(11.64, -29.4) * mm, "mid": v(11.67, -29.49) * mm, "end": v(11.76, -29.52) * mm});
            skPoint(sketch, "E139.visualSharp", {"position": v(12.66, -29.52) * mm});
            skArc(sketch, "E139.filletArc", {"start": v(12.54, -29.52) * mm, "mid": v(12.62, -29.49) * mm, "end": v(12.66, -29.4) * mm});
            skPoint(sketch, "E140.visualSharp", {"position": v(4.27, -28.5) * mm});
            skArc(sketch, "E140.filletArc", {"start": v(4.39, -28.5) * mm, "mid": v(4.3, -28.54) * mm, "end": v(4.27, -28.62) * mm});
            skPoint(sketch, "E141.visualSharp", {"position": v(6.33, -28.5) * mm});
            skArc(sketch, "E141.filletArc", {"start": v(6.22, -28.5) * mm, "mid": v(6.3, -28.47) * mm, "end": v(6.33, -28.39) * mm});
            skPoint(sketch, "E142.visualSharp", {"position": v(6.33, -27.49) * mm});
            skArc(sketch, "E142.filletArc", {"start": v(6.33, -27.6) * mm, "mid": v(6.3, -27.52) * mm, "end": v(6.22, -27.49) * mm});
            skPoint(sketch, "E143.visualSharp", {"position": v(4.27, -27.49) * mm});
            skArc(sketch, "E143.filletArc", {"start": v(4.27, -27.37) * mm, "mid": v(4.3, -27.45) * mm, "end": v(4.39, -27.49) * mm});
            skPoint(sketch, "E144.visualSharp", {"position": v(3.26, -26.47) * mm});
            skArc(sketch, "E144.filletArc", {"start": v(3.37, -26.47) * mm, "mid": v(3.3, -26.5) * mm, "end": v(3.26, -26.59) * mm});
            skPoint(sketch, "E145.visualSharp", {"position": v(1.2, -27.49) * mm});
            skArc(sketch, "E145.filletArc", {"start": v(1.31, -27.49) * mm, "mid": v(1.23, -27.52) * mm, "end": v(1.2, -27.6) * mm});
            skPoint(sketch, "E146.visualSharp", {"position": v(3.26, -28.5) * mm});
            skArc(sketch, "E146.filletArc", {"start": v(3.26, -28.62) * mm, "mid": v(3.22, -28.54) * mm, "end": v(3.14, -28.5) * mm});
            skPoint(sketch, "E147.visualSharp", {"position": v(3.26, -29.52) * mm});
            skArc(sketch, "E147.filletArc", {"start": v(3.26, -29.4) * mm, "mid": v(3.3, -29.49) * mm, "end": v(3.37, -29.52) * mm});
            skPoint(sketch, "E148.visualSharp", {"position": v(4.27, -29.52) * mm});
            skArc(sketch, "E148.filletArc", {"start": v(4.16, -29.52) * mm, "mid": v(4.24, -29.49) * mm, "end": v(4.27, -29.4) * mm});
            skPoint(sketch, "E149.visualSharp", {"position": v(1.2, -28.5) * mm});
            skArc(sketch, "E149.filletArc", {"start": v(1.2, -28.39) * mm, "mid": v(1.23, -28.47) * mm, "end": v(1.31, -28.5) * mm});
            skSolve(sketch);
        }
        {
            var Q0;
            {Q0=qUnion([makeQuery(id+"F18.imprint","IMPRINT",FACE,{"disambiguationData":[TD([[makeQuery(id+"F18.imprint","IMPRINT",EDGE,{"derivedFrom":sQuery(id+"F18.wireOp",EDGE,"E86.rect.bottom")}),-1.0]])]}),makeQuery(id+"F18.imprint","IMPRINT",FACE,{"disambiguationData":[TD([[makeQuery(id+"F18.imprint","IMPRINT",EDGE,{"derivedFrom":sQuery(id+"F18.wireOp",EDGE,"E88.2.MirrorCS")}),1.0]])]}),makeQuery(id+"F18.imprint","IMPRINT",FACE,{"disambiguationData":[TD([[makeQuery(id+"F18.imprint","IMPRINT",EDGE,{"derivedFrom":sQuery(id+"F18.wireOp",EDGE,"E88.3.MirrorCS")}),1.0]])]}),makeQuery(id+"F18.imprint","IMPRINT",FACE,{"disambiguationData":[TD([[makeQuery(id+"F18.imprint","IMPRINT",EDGE,{"derivedFrom":sQuery(id+"F18.wireOp",EDGE,"E84.rect.bottom")}),-1.0]])]})]);}
            extrude(context, id + "F19", {"entities" : qUnion([Q0]), "operationType" : NewBodyOperationType.REMOVE, "oppositeDirection" : true, "depth" : 0.76 * mm});
        }
        {
            var Q0;
            Q0=makeQuery(id+"F17.opExtrude","CAP_EDGE",EDGE,{"disambiguationData":[OSD([sQuery(id+"F16.wireOp",EDGE,"E79")])],"isStart":false});
            var Q1;
            Q1=makeQuery(id+"F17.opExtrude","CAP_EDGE",EDGE,{"disambiguationData":[OSD([sQuery(id+"F16.wireOp",EDGE,"E80")])],"isStart":false});
            var Q2;
            Q2=makeQuery(id+"F17.opExtrude","CAP_EDGE",EDGE,{"disambiguationData":[OSD([sQuery(id+"F16.wireOp",EDGE,"E82.0.MirrorC")])],"isStart":false});
            var Q3;
            Q3=makeQuery(id+"F17.opExtrude","CAP_EDGE",EDGE,{"disambiguationData":[OSD([sQuery(id+"F16.wireOp",EDGE,"E83.0.MirrorC")])],"isStart":false});
            fillet(context, id + "F20", {"entities" : qUnion([Q0, Q1, Q2, Q3]), "radius" : 1.02 * mm, "tangentPropagation" : true, "allowEdgeOverflow" : false});
        }
    });
